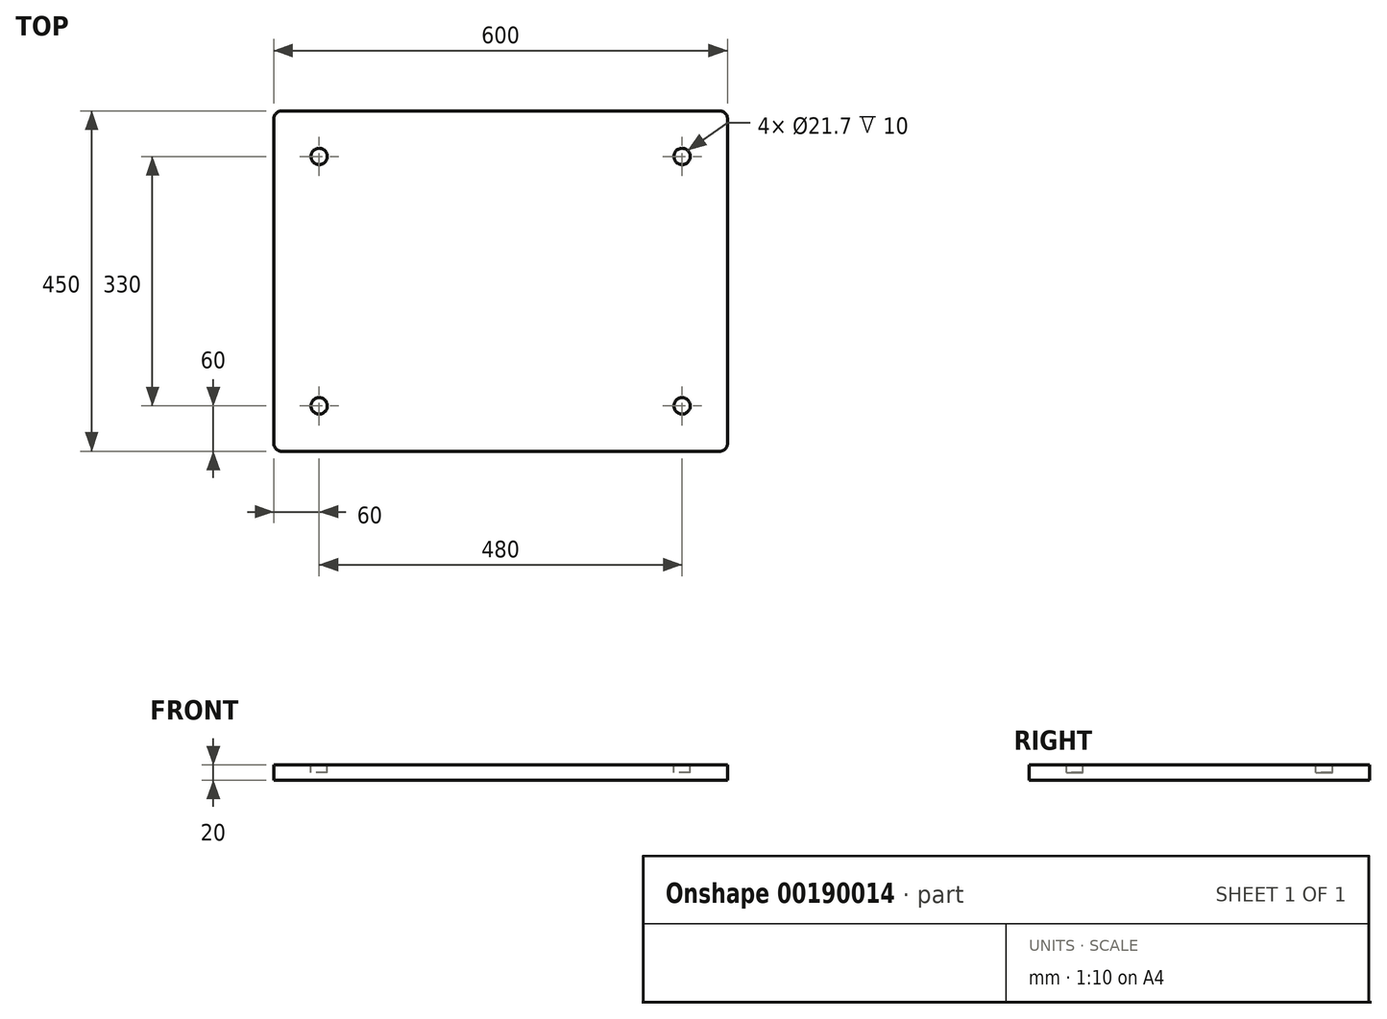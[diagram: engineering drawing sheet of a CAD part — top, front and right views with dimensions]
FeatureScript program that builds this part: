
annotation { "Feature Type Name" : "Feature", "Feature Type Description" : "" }
export const myFeature = defineFeature(function(context is Context, id is Id, definition is map)
    precondition{}
    {
        {
            var Q0;
            Q0=qCreatedBy(makeId("Top.planeOp"),FACE);
            var sketch = newSketch(context, id + "F0", { "sketchPlane" : qUnion([Q0])});
            skLineSegment(sketch, "E0.bottom", {"start": v(290, -225) * mm, "end": v(-290, -225) * mm});
            skLineSegment(sketch, "E0.top", {"start": v(290, 225) * mm, "end": v(-290, 225) * mm});
            skLineSegment(sketch, "E0.left", {"start": v(300, -215) * mm, "end": v(300, 215) * mm});
            skLineSegment(sketch, "E0.right", {"start": v(-300, -215) * mm, "end": v(-300, 215) * mm});
            skPoint(sketch, "E1.visualSharp", {"position": v(300, -225) * mm});
            skArc(sketch, "E1.filletArc", {"start": v(290, -225) * mm, "mid": v(297.07, -222.07) * mm, "end": v(300, -215) * mm});
            skPoint(sketch, "E2.visualSharp", {"position": v(300, 225) * mm});
            skArc(sketch, "E2.filletArc", {"start": v(300, 215) * mm, "mid": v(297.07, 222.07) * mm, "end": v(290, 225) * mm});
            skPoint(sketch, "E3.visualSharp", {"position": v(-300, 225) * mm});
            skArc(sketch, "E3.filletArc", {"start": v(-290, 225) * mm, "mid": v(-297.07, 222.07) * mm, "end": v(-300, 215) * mm});
            skPoint(sketch, "E4.visualSharp", {"position": v(-300, -225) * mm});
            skArc(sketch, "E4.filletArc", {"start": v(-300, -215) * mm, "mid": v(-297.07, -222.07) * mm, "end": v(-290, -225) * mm});
            skSolve(sketch);
        }
        {
            var Q0;
            Q0=makeQuery(id+"F0.imprint","IMPRINT",FACE,{"disambiguationData":[TD([[makeQuery(id+"F0.imprint","IMPRINT",EDGE,{"derivedFrom":sQuery(id+"F0.wireOp",EDGE,"E0.bottom")}),-1.0]])]});
            extrude(context, id + "F1", {"entities" : qUnion([Q0]), "depth" : 20 * mm});
        }
        {
            var Q0;
            Q0=makeQuery(id+"F1.opExtrude","CAP_FACE",FACE,{"disambiguationData":[OSD([sQuery(id+"F0.wireOp",EDGE,"E0.bottom"),sQuery(id+"F0.wireOp",EDGE,"E0.top"),sQuery(id+"F0.wireOp",EDGE,"E0.left"),sQuery(id+"F0.wireOp",EDGE,"E0.right"),sQuery(id+"F0.wireOp",EDGE,"E1.filletArc"),sQuery(id+"F0.wireOp",EDGE,"E2.filletArc"),sQuery(id+"F0.wireOp",EDGE,"E3.filletArc"),sQuery(id+"F0.wireOp",EDGE,"E4.filletArc")])],"isStart":false});
            var sketch = newSketch(context, id + "F2", { "sketchPlane" : qUnion([Q0])});
            skLineSegment(sketch, "E5.0.0", {"start": v(290, -225) * mm, "end": v(-290, -225) * mm});
            skArc(sketch, "E5.0.1", {"start": v(-290, -225) * mm, "mid": v(-297.07, -222.07) * mm, "end": v(-300, -215) * mm});
            skLineSegment(sketch, "E5.0.2", {"start": v(-300, -215) * mm, "end": v(-300, 215) * mm});
            skArc(sketch, "E5.0.3", {"start": v(-300, 215) * mm, "mid": v(-297.07, 222.07) * mm, "end": v(-290, 225) * mm});
            skLineSegment(sketch, "E5.0.4", {"start": v(-290, 225) * mm, "end": v(290, 225) * mm});
            skArc(sketch, "E5.0.5", {"start": v(290, 225) * mm, "mid": v(297.07, 222.07) * mm, "end": v(300, 215) * mm});
            skLineSegment(sketch, "E5.0.6", {"start": v(300, 215) * mm, "end": v(300, -215) * mm});
            skArc(sketch, "E5.0.7", {"start": v(300, -215) * mm, "mid": v(297.07, -222.07) * mm, "end": v(290, -225) * mm});
            skCircle(sketch, "E6", {"center": v(-240, -165) * mm, "radius": 10.85 * mm});
            skCircle(sketch, "E7", {"center": v(240, -165) * mm, "radius": 10.85 * mm});
            skCircle(sketch, "E8", {"center": v(-240, 165) * mm, "radius": 10.85 * mm});
            skCircle(sketch, "E9", {"center": v(240, 165) * mm, "radius": 10.85 * mm});
            skSolve(sketch);
        }
        {
            var Q0;
            Q0=makeQuery(id+"F2.imprint","IMPRINT",FACE,{"disambiguationData":[TD([[makeQuery(id+"F2.imprint","IMPRINT",EDGE,{"derivedFrom":sQuery(id+"F2.wireOp",EDGE,"E8")}),1.0]])]});
            var Q1;
            Q1=makeQuery(id+"F2.imprint","IMPRINT",FACE,{"disambiguationData":[TD([[makeQuery(id+"F2.imprint","IMPRINT",EDGE,{"derivedFrom":sQuery(id+"F2.wireOp",EDGE,"E9")}),1.0]])]});
            var Q2;
            Q2=makeQuery(id+"F2.imprint","IMPRINT",FACE,{"disambiguationData":[TD([[makeQuery(id+"F2.imprint","IMPRINT",EDGE,{"derivedFrom":sQuery(id+"F2.wireOp",EDGE,"E7")}),1.0]])]});
            var Q3;
            Q3=makeQuery(id+"F2.imprint","IMPRINT",FACE,{"disambiguationData":[TD([[makeQuery(id+"F2.imprint","IMPRINT",EDGE,{"derivedFrom":sQuery(id+"F2.wireOp",EDGE,"E6")}),1.0]])]});
            extrude(context, id + "F3", {"entities" : qUnion([Q0, Q1, Q2, Q3]), "operationType" : NewBodyOperationType.REMOVE, "oppositeDirection" : true, "depth" : 10 * mm});
        }
    });
